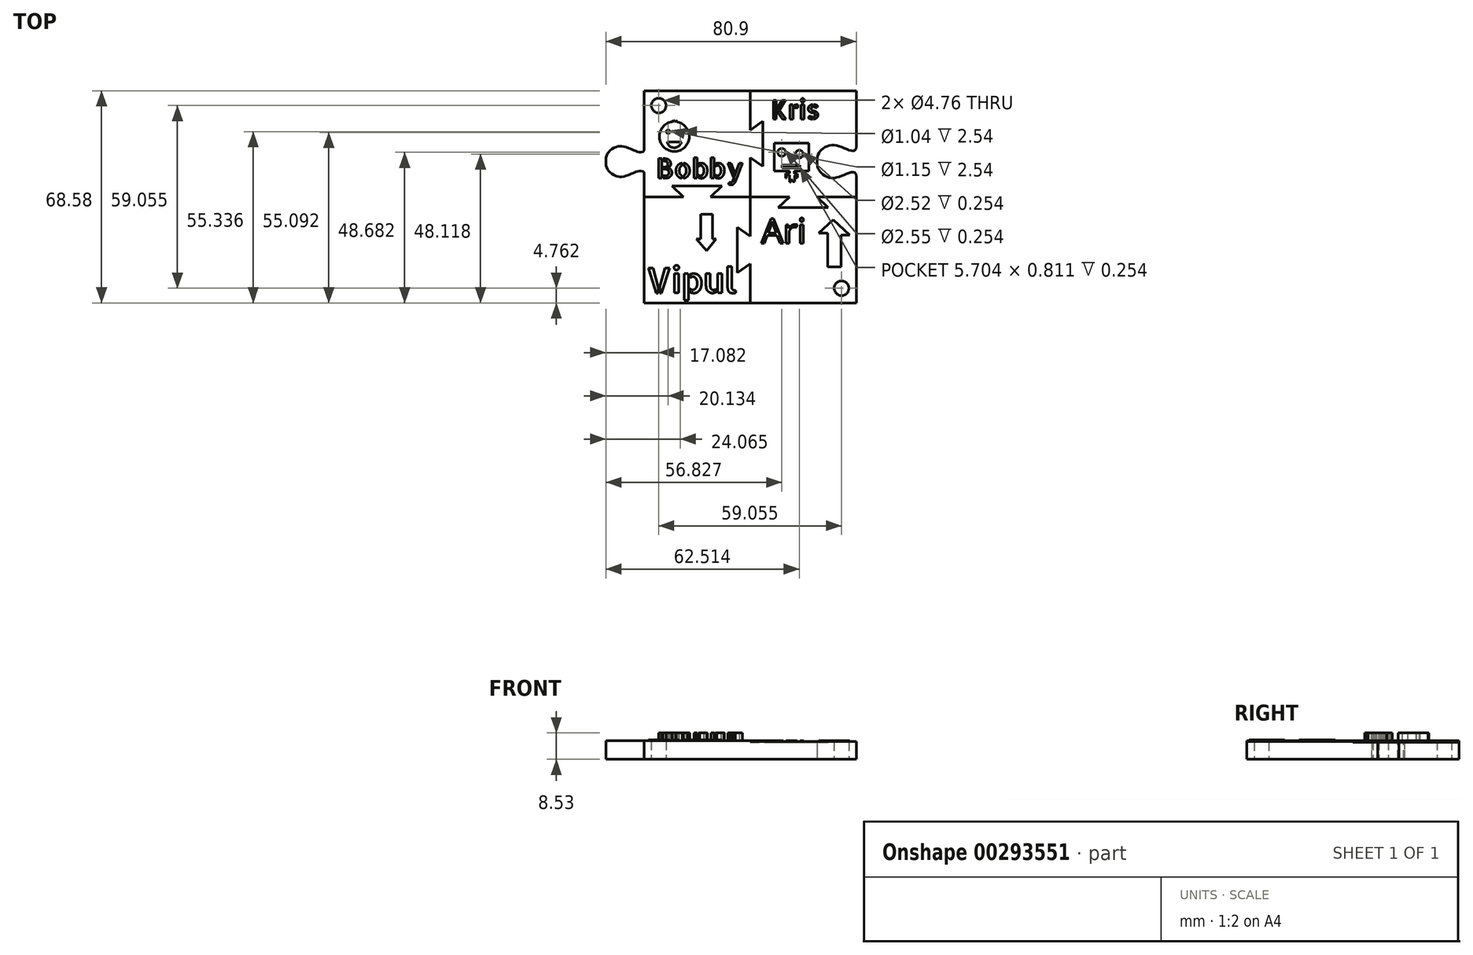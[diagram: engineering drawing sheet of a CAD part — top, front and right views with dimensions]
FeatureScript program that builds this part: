
annotation { "Feature Type Name" : "Feature", "Feature Type Description" : "" }
export const myFeature = defineFeature(function(context is Context, id is Id, definition is map)
    precondition{}
    {
        {
            var Q0;
            Q0=qCreatedBy(makeId("Top.planeOp"),FACE);
            var sketch = newSketch(context, id + "F0", { "sketchPlane" : qUnion([Q0])});
            skLineSegment(sketch, "E0.bottom", {"start": v(34.3, 34.3) * mm, "end": v(-34.3, 34.3) * mm});
            skLineSegment(sketch, "E0.top", {"start": v(34.3, -34.3) * mm, "end": v(-34.3, -34.3) * mm});
            skLineSegment(sketch, "E0.left", {"start": v(34.3, 34.3) * mm, "end": v(34.3, -34.3) * mm});
            skLineSegment(sketch, "E0.right", {"start": v(-34.3, 34.3) * mm, "end": v(-34.3, -34.3) * mm});
            skPoint(sketch, "E0.middle", {"position": v(0, 0) * mm});
            skCircle(sketch, "E1", {"center": v(-29.53, 29.53) * mm, "radius": 2.38 * mm});
            skCircle(sketch, "E2.MirrorC", {"center": v(29.53, -29.53) * mm, "radius": 2.38 * mm});
            skSolve(sketch);
        }
        {
            var Q0;
            Q0=qSketchRegion(id+"F0",true);
            extrude(context, id + "F1", {"entities" : qUnion([Q0]), "depth" : 3.17 * mm});
        }
        {
            var Q0;
            Q0=qCreatedBy(makeId("Top.planeOp"),FACE);
            var sketch = newSketch(context, id + "F2", { "sketchPlane" : qUnion([Q0])});
            skPoint(sketch, "E3", {"position": v(-34.3, 16.33) * mm});
            skPoint(sketch, "E4", {"position": v(-36.2, 14.99) * mm});
            skPoint(sketch, "E5", {"position": v(-41.66, 16.76) * mm});
            skPoint(sketch, "E6", {"position": v(-45.72, 14.99) * mm});
            skPoint(sketch, "E7", {"position": v(-47, 11.43) * mm});
            skFitSpline(sketch, "E8", {"points": [v(-34.3, 16.33) * mm, v(-36.2, 14.99) * mm, v(-41.66, 16.76) * mm, v(-45.72, 14.99) * mm, v(-47, 11.43) * mm], "startDerivative": vector(0, -24.54) * mm, "endDerivative": vector(0, -20.15) * mm});
            skLineSegment(sketch, "E9", {"start": v(-47, 11.43) * mm, "end": v(-29.95, 11.43) * mm, "construction": true});
            skFitSpline(sketch, "E10.MirrorCS", {"points": [v(-34.3, 6.53) * mm, v(-36.2, 7.87) * mm, v(-41.66, 6.1) * mm, v(-45.72, 7.87) * mm, v(-47, 11.43) * mm], "startDerivative": vector(0, 24.54) * mm, "endDerivative": vector(0, 20.15) * mm});
            skLineSegment(sketch, "E11", {"start": v(-34.3, 16.33) * mm, "end": v(-34.3, 6.53) * mm, "construction": true});
            skFitSpline(sketch, "E12.MirrorCS", {"points": [v(-34.3, 16.33) * mm, v(-32.39, 14.99) * mm, v(-26.92, 16.76) * mm, v(-22.86, 14.99) * mm, v(-21.59, 11.43) * mm], "startDerivative": vector(0, -24.54) * mm, "endDerivative": vector(0, -20.15) * mm});
            skFitSpline(sketch, "E13.MirrorCS", {"points": [v(-34.3, 6.53) * mm, v(-32.39, 7.87) * mm, v(-26.92, 6.1) * mm, v(-22.86, 7.87) * mm, v(-21.59, 11.43) * mm], "startDerivative": vector(0, 24.54) * mm, "endDerivative": vector(0, 20.15) * mm});
            skFitSpline(sketch, "E14.0", {"points": [v(-33.9, 6.53) * mm, v(-33.9, 6.8) * mm, v(-33.96, 7.3) * mm, v(-34.16, 7.77) * mm, v(-34.42, 8.07) * mm, v(-34.73, 8.28) * mm, v(-35.16, 8.4) * mm, v(-35.7, 8.38) * mm, v(-36.22, 8.27) * mm, v(-36.76, 8.1) * mm, v(-37.5, 7.83) * mm, v(-38.44, 7.42) * mm, v(-39.6, 6.94) * mm, v(-40.54, 6.64) * mm, v(-41.28, 6.5) * mm, v(-41.8, 6.46) * mm, v(-42.32, 6.5) * mm, v(-43, 6.62) * mm, v(-43.8, 6.91) * mm, v(-44.68, 7.44) * mm, v(-45.29, 7.96) * mm, v(-45.69, 8.4) * mm, v(-46.02, 8.85) * mm, v(-46.33, 9.45) * mm, v(-46.56, 10.3) * mm, v(-46.6, 11.03) * mm, v(-46.6, 11.43) * mm]});
            skFitSpline(sketch, "E14.1", {"points": [v(-33.9, 16.33) * mm, v(-33.9, 16.05) * mm, v(-33.96, 15.56) * mm, v(-34.16, 15.09) * mm, v(-34.42, 14.8) * mm, v(-34.73, 14.58) * mm, v(-35.16, 14.46) * mm, v(-35.7, 14.48) * mm, v(-36.22, 14.6) * mm, v(-36.76, 14.76) * mm, v(-37.5, 15.03) * mm, v(-38.44, 15.44) * mm, v(-39.6, 15.92) * mm, v(-40.54, 16.22) * mm, v(-41.28, 16.36) * mm, v(-41.8, 16.4) * mm, v(-42.32, 16.37) * mm, v(-43, 16.24) * mm, v(-43.8, 15.95) * mm, v(-44.68, 15.42) * mm, v(-45.29, 14.9) * mm, v(-45.69, 14.46) * mm, v(-46.02, 14.01) * mm, v(-46.33, 13.41) * mm, v(-46.56, 12.55) * mm, v(-46.6, 11.83) * mm, v(-46.6, 11.43) * mm]});
            skLineSegment(sketch, "E15", {"start": v(-34.3, 16.33) * mm, "end": v(-34.3, 6.53) * mm});
            skLineSegment(sketch, "E16", {"start": v(-34.3, 7.92) * mm, "end": v(-34.3, 14.94) * mm});
            skFitSpline(sketch, "E17.MirrorCS", {"points": [v(34.3, 16.33) * mm, v(32.39, 14.99) * mm, v(26.92, 16.76) * mm, v(22.86, 14.99) * mm, v(21.59, 11.43) * mm], "startDerivative": vector(0, -24.54) * mm, "endDerivative": vector(0, -20.15) * mm});
            skFitSpline(sketch, "E18.MirrorCS", {"points": [v(34.3, 6.53) * mm, v(32.39, 7.87) * mm, v(26.92, 6.1) * mm, v(22.86, 7.87) * mm, v(21.59, 11.43) * mm], "startDerivative": vector(0, 24.54) * mm, "endDerivative": vector(0, 20.15) * mm});
            skLineSegment(sketch, "E19", {"start": v(34.3, 16.33) * mm, "end": v(39.12, 16.33) * mm});
            skLineSegment(sketch, "E20", {"start": v(39.12, 16.33) * mm, "end": v(39.12, 6.53) * mm});
            skLineSegment(sketch, "E21", {"start": v(39.12, 6.53) * mm, "end": v(34.3, 6.53) * mm});
            skSolve(sketch);
        }
        {
            var Q0;
            Q0=makeQuery(id+"F2.imprint","IMPRINT",FACE,{"disambiguationData":[TD([[makeQuery(id+"F2.imprint","IMPRINT",EDGE,{"derivedFrom":sQuery(id+"F2.wireOp",EDGE,"E14.0")}),-1.0]])]});
            var Q1;
            Q1=makeQuery(id+"F1.opExtrude","CAP_FACE",FACE,{"disambiguationData":[OSD([sQuery(id+"F0.wireOp",EDGE,"E0.bottom"),sQuery(id+"F0.wireOp",EDGE,"E0.top"),sQuery(id+"F0.wireOp",EDGE,"E0.left"),sQuery(id+"F0.wireOp",EDGE,"E0.right"),sQuery(id+"F0.wireOp",EDGE,"E1"),sQuery(id+"F0.wireOp",EDGE,"e1648c08-8adf-473f-9b64-c467cf328ef90.MirrorC"),sQuery(id+"F0.wireOp",EDGE,"1cdcda55-2210-49d8-b5f0-9198a802923b0.MirrorC"),sQuery(id+"F0.wireOp",EDGE,"E2.MirrorC")])],"isStart":false});
            extrude(context, id + "F3", {"entities" : qUnion([Q0]), "operationType" : NewBodyOperationType.ADD, "endBound" : BoundingType.UP_TO_SURFACE, "endBoundEntityFace" : qUnion([Q1]), "depth" : 25.4 * mm});
        }
        {
            var Q0;
            Q0=qCreatedBy(makeId("Right.planeOp"),FACE);
            var sketch = newSketch(context, id + "F4", { "sketchPlane" : qUnion([Q0])});
            skLineSegment(sketch, "E22", {"start": v(0, -65.87) * mm, "end": v(0, 47.63) * mm});
            skSolve(sketch);
        }
        {
            var Q0;
            Q0=makeQuery(id+"F2.imprint","IMPRINT",FACE,{"disambiguationData":[TD([[makeQuery(id+"F2.imprint","IMPRINT",EDGE,{"derivedFrom":sQuery(id+"F2.wireOp",EDGE,"E17.MirrorCS")}),1.0]])]});
            extrude(context, id + "F5", {"entities" : qUnion([Q0]), "operationType" : NewBodyOperationType.REMOVE, "endBound" : BoundingType.THROUGH_ALL, "depth" : 25.4 * mm});
        }
        {
            var Q0;
            {var subQ0=sQuery(id+"F0.wireOp",EDGE,"E2.MirrorC");var subQ1=sQuery(id+"F0.wireOp",EDGE,"E1");var subQ2=sQuery(id+"F0.wireOp",EDGE,"E0.right");var subQ3=sQuery(id+"F0.wireOp",EDGE,"E0.left");var subQ4=sQuery(id+"F0.wireOp",EDGE,"E0.top");var subQ5=sQuery(id+"F0.wireOp",EDGE,"E0.bottom");Q0=makeQuery(id+"FDfX84p6046V9zH_1.3.F3.boolean.opBoolean","MERGE",FACE,{"derivedFrom":[makeQuery(id+"FDfX84p6046V9zH_1.2.F3.boolean.opBoolean","MERGE",FACE,{"derivedFrom":[makeQuery(id+"FDfX84p6046V9zH_1.1.F3.boolean.opBoolean","MERGE",FACE,{"derivedFrom":[makeQuery(id+"F3.boolean.opBoolean","MERGE",FACE,{"derivedFrom":[makeQuery(id+"F1.opExtrude","CAP_FACE",FACE,{"disambiguationData":[OSD([subQ5,subQ4,subQ3,subQ2,subQ1,subQ0])],"isStart":false}),makeQuery(id+"F3.opExtrude","CAP_FACE",FACE,{"disambiguationData":[OSD([subQ5,subQ4,subQ3,subQ2,subQ1,subQ0])],"isStart":false})]}),makeQuery(id+"FDfX84p6046V9zH_1.1.F3.opExtrude","CAP_FACE",FACE,{"disambiguationData":[OSD([subQ5,subQ4,subQ3,subQ2,subQ1,subQ0])],"isStart":false})]}),makeQuery(id+"FDfX84p6046V9zH_1.2.F3.opExtrude","CAP_FACE",FACE,{"disambiguationData":[OSD([subQ5,subQ4,subQ3,subQ2,subQ1,subQ0])],"isStart":false})]}),makeQuery(id+"FDfX84p6046V9zH_1.3.F3.opExtrude","CAP_FACE",FACE,{"disambiguationData":[OSD([subQ5,subQ4,subQ3,subQ2,subQ1,subQ0])],"isStart":false})]});}
            var sketch = newSketch(context, id + "F6", { "sketchPlane" : qUnion([Q0])});
            skLineSegment(sketch, "E23", {"start": v(-34.3, 0) * mm, "end": v(-21.58, 0) * mm});
            skLineSegment(sketch, "E24", {"start": v(-21.58, 0) * mm, "end": v(-25.25, 3.52) * mm});
            skLineSegment(sketch, "E25", {"start": v(0, 0) * mm, "end": v(-12.73, 0) * mm});
            skLineSegment(sketch, "E26", {"start": v(-12.73, 0) * mm, "end": v(-9.11, 3.52) * mm});
            skLineSegment(sketch, "E27", {"start": v(-9.11, 3.52) * mm, "end": v(-25.25, 3.52) * mm});
            skLineSegment(sketch, "E28.MirrorCS", {"start": v(34.3, 0) * mm, "end": v(21.58, 0) * mm});
            skLineSegment(sketch, "E29.MirrorCS", {"start": v(0, 0) * mm, "end": v(12.73, 0) * mm});
            skLineSegment(sketch, "E30.MirrorCS", {"start": v(9.11, -3.52) * mm, "end": v(25.25, -3.52) * mm});
            skLineSegment(sketch, "E31.MirrorCS", {"start": v(12.73, 0) * mm, "end": v(9.11, -3.52) * mm});
            skLineSegment(sketch, "E32.MirrorCS", {"start": v(21.58, 0) * mm, "end": v(25.25, -3.52) * mm});
            skPoint(sketch, "E33.MirrorCS.start.orphan", {"position": v(-12.73, 0) * mm});
            skPoint(sketch, "E34.MirrorCS.start.orphan", {"position": v(-21.58, 0) * mm});
            skLineSegment(sketch, "E35", {"start": v(0, 34.3) * mm, "end": v(0, 21.6) * mm});
            skLineSegment(sketch, "E36", {"start": v(0, 21.6) * mm, "end": v(4.16, 24.51) * mm});
            skLineSegment(sketch, "E37", {"start": v(0, 0) * mm, "end": v(0, 12.7) * mm});
            skLineSegment(sketch, "E38", {"start": v(0, 12.7) * mm, "end": v(4.16, 9.86) * mm});
            skLineSegment(sketch, "E39", {"start": v(4.16, 9.86) * mm, "end": v(4.16, 24.51) * mm});
            skLineSegment(sketch, "E40.MirrorCS", {"start": v(0, 0) * mm, "end": v(0, -12.7) * mm});
            skLineSegment(sketch, "E41.MirrorCS", {"start": v(0, -34.3) * mm, "end": v(0, -21.6) * mm});
            skLineSegment(sketch, "E42.MirrorCS", {"start": v(0, -12.7) * mm, "end": v(-4.16, -9.86) * mm});
            skLineSegment(sketch, "E43.MirrorCS", {"start": v(-4.16, -9.86) * mm, "end": v(-4.16, -24.51) * mm});
            skLineSegment(sketch, "E44.MirrorCS", {"start": v(0, -21.6) * mm, "end": v(-4.16, -24.51) * mm});
            skPoint(sketch, "E45.MirrorCS.start.orphan", {"position": v(0, -12.7) * mm});
            skPoint(sketch, "E46.MirrorCS.start.orphan", {"position": v(0, -21.6) * mm});
            skSolve(sketch);
        }
        {
            var Q0;
            {var subQ1=sQuery(id+"F6.wireOp",EDGE,"E28.MirrorCS");Q0=makeQuery(id+"F6.imprint","IMPRINT",FACE,{"disambiguationData":[TD([[makeQuery(id+"F6.imprint","IMPRINT",EDGE,{"derivedFrom":subQ1}),1.0]])]});}
            extrude(context, id + "F7", {"entities" : qUnion([Q0]), "operationType" : NewBodyOperationType.ADD, "depth" : 2.54 * mm});
        }
        {
            var Q0;
            {var subQ22=sQuery(id+"F6.wireOp",EDGE,"E23");Q0=makeQuery(id+"F6.imprint","IMPRINT",FACE,{"disambiguationData":[TD([[makeQuery(id+"F6.imprint","IMPRINT",EDGE,{"derivedFrom":subQ22}),-1.0]])]});}
            extrude(context, id + "F8", {"entities" : qUnion([Q0]), "operationType" : NewBodyOperationType.ADD, "depth" : 2.8 * mm});
        }
        {
            var Q0;
            {var subQ21=sQuery(id+"F6.wireOp",EDGE,"E23");Q0=makeQuery(id+"F6.imprint","IMPRINT",FACE,{"disambiguationData":[TD([[makeQuery(id+"F6.imprint","IMPRINT",EDGE,{"derivedFrom":subQ21}),1.0]])]});}
            extrude(context, id + "F9", {"entities" : qUnion([Q0]), "operationType" : NewBodyOperationType.ADD, "depth" : 2.82 * mm});
        }
        {
            var Q0;
            {var subQ0=sQuery(id+"F0.wireOp",EDGE,"E2.MirrorC");var subQ1=sQuery(id+"F0.wireOp",EDGE,"E1");var subQ2=sQuery(id+"F0.wireOp",EDGE,"E0.right");var subQ3=sQuery(id+"F0.wireOp",EDGE,"E0.left");var subQ4=sQuery(id+"F0.wireOp",EDGE,"E0.top");var subQ5=sQuery(id+"F0.wireOp",EDGE,"E0.bottom");Q0=makeQuery(id+"FDfX84p6046V9zH_1.3.F3.boolean.opBoolean","MERGE",FACE,{"derivedFrom":[makeQuery(id+"FDfX84p6046V9zH_1.2.F3.boolean.opBoolean","MERGE",FACE,{"derivedFrom":[makeQuery(id+"FDfX84p6046V9zH_1.1.F3.boolean.opBoolean","MERGE",FACE,{"derivedFrom":[makeQuery(id+"F3.boolean.opBoolean","MERGE",FACE,{"derivedFrom":[makeQuery(id+"F1.opExtrude","CAP_FACE",FACE,{"disambiguationData":[OSD([subQ5,subQ4,subQ3,subQ2,subQ1,subQ0])],"isStart":false}),makeQuery(id+"F3.opExtrude","CAP_FACE",FACE,{"disambiguationData":[OSD([subQ5,subQ4,subQ3,subQ2,subQ1,subQ0])],"isStart":false})]}),makeQuery(id+"FDfX84p6046V9zH_1.1.F3.opExtrude","CAP_FACE",FACE,{"disambiguationData":[OSD([subQ5,subQ4,subQ3,subQ2,subQ1,subQ0])],"isStart":false})]}),makeQuery(id+"FDfX84p6046V9zH_1.2.F3.opExtrude","CAP_FACE",FACE,{"disambiguationData":[OSD([subQ5,subQ4,subQ3,subQ2,subQ1,subQ0])],"isStart":false})]}),makeQuery(id+"FDfX84p6046V9zH_1.3.F3.opExtrude","CAP_FACE",FACE,{"disambiguationData":[OSD([subQ5,subQ4,subQ3,subQ2,subQ1,subQ0])],"isStart":false})]});}
            extrude(context, id + "F10", {"entities" : qUnion([Q0]), "operationType" : NewBodyOperationType.ADD, "depth" : 2.3 * mm});
        }
        {
            var Q0;
            Q0=makeQuery(id+"F8.opExtrude","CAP_FACE",FACE,{"disambiguationData":[OSD([sQuery(id+"F0.wireOp",EDGE,"E0.bottom"),sQuery(id+"F0.wireOp",EDGE,"E0.top"),sQuery(id+"F0.wireOp",EDGE,"E0.left"),sQuery(id+"F0.wireOp",EDGE,"E0.right"),sQuery(id+"F0.wireOp",EDGE,"E1"),sQuery(id+"F0.wireOp",EDGE,"E2.MirrorC"),sQuery(id+"F2.wireOp",EDGE,"E14.0"),sQuery(id+"F2.wireOp",EDGE,"E14.1"),sQuery(id+"F2.wireOp",EDGE,"E17.MirrorCS"),sQuery(id+"F2.wireOp",EDGE,"E18.MirrorCS"),sQuery(id+"F6.wireOp",EDGE,"E23"),sQuery(id+"F6.wireOp",EDGE,"E24"),sQuery(id+"F6.wireOp",EDGE,"E25"),sQuery(id+"F6.wireOp",EDGE,"E26"),sQuery(id+"F6.wireOp",EDGE,"E27"),sQuery(id+"F6.wireOp",EDGE,"E40.MirrorCS"),sQuery(id+"F6.wireOp",EDGE,"E41.MirrorCS"),sQuery(id+"F6.wireOp",EDGE,"E42.MirrorCS"),sQuery(id+"F6.wireOp",EDGE,"E43.MirrorCS"),sQuery(id+"F6.wireOp",EDGE,"E44.MirrorCS")])],"isStart":false});
            var sketch = newSketch(context, id + "F11", { "sketchPlane" : qUnion([Q0])});
            skText(sketch, "E47", { "text": "Vipul", "fontName": "AllertaStencil-Regular.ttf"});
            skLineSegment(sketch, "E48", {"start": v(-15.92, -5.68) * mm, "end": v(-12.2, -5.68) * mm});
            skLineSegment(sketch, "E49", {"start": v(-12.2, -5.68) * mm, "end": v(-12.2, -13.66) * mm});
            skLineSegment(sketch, "E50", {"start": v(-15.92, -5.68) * mm, "end": v(-15.92, -13.66) * mm});
            skLineSegment(sketch, "E51", {"start": v(-15.92, -13.66) * mm, "end": v(-17.34, -13.66) * mm});
            skLineSegment(sketch, "E52", {"start": v(-17.34, -13.66) * mm, "end": v(-14.06, -17.38) * mm});
            skPoint(sketch, "E52.endSnap0", {"position": v(-14.06, -5.68) * mm});
            skLineSegment(sketch, "E53", {"start": v(-14.06, -17.38) * mm, "end": v(-11, -13.66) * mm});
            skLineSegment(sketch, "E54", {"start": v(-11, -13.66) * mm, "end": v(-12.2, -13.66) * mm});
            const initialGuessF11  = {"E47": [-0.03353, -0.03106, 1, 0, 0.0081]};
            skSetInitialGuess(sketch, initialGuessF11);
            skSolve(sketch);
        }
        {
            var Q0;
            Q0 = qSketchRegion(id + "F11", true);
            extrude(context, id + "F12", {"entities" : qUnion([Q0]), "operationType" : NewBodyOperationType.ADD, "depth" : 0.25 * mm});
        }
        {
            var Q0;
            Q0=makeQuery(id+"F9.opExtrude","CAP_FACE",FACE,{"disambiguationData":[OSD([sQuery(id+"F0.wireOp",EDGE,"E0.bottom"),sQuery(id+"F0.wireOp",EDGE,"E0.top"),sQuery(id+"F0.wireOp",EDGE,"E0.left"),sQuery(id+"F0.wireOp",EDGE,"E0.right"),sQuery(id+"F0.wireOp",EDGE,"E1"),sQuery(id+"F0.wireOp",EDGE,"E2.MirrorC"),sQuery(id+"F2.wireOp",EDGE,"E14.0"),sQuery(id+"F2.wireOp",EDGE,"E14.1"),sQuery(id+"F2.wireOp",EDGE,"E17.MirrorCS"),sQuery(id+"F2.wireOp",EDGE,"E18.MirrorCS"),sQuery(id+"F6.wireOp",EDGE,"E23"),sQuery(id+"F6.wireOp",EDGE,"E24"),sQuery(id+"F6.wireOp",EDGE,"E25"),sQuery(id+"F6.wireOp",EDGE,"E26"),sQuery(id+"F6.wireOp",EDGE,"E27"),sQuery(id+"F6.wireOp",EDGE,"E35"),sQuery(id+"F6.wireOp",EDGE,"E36"),sQuery(id+"F6.wireOp",EDGE,"E37"),sQuery(id+"F6.wireOp",EDGE,"E38"),sQuery(id+"F6.wireOp",EDGE,"E39")])],"isStart":false});
            var sketch = newSketch(context, id + "F13", { "sketchPlane" : qUnion([Q0])});
            skText(sketch, "E55", { "text": "Bobby", "fontName": "AllertaStencil-Regular.ttf"});
            skCircle(sketch, "E56", {"center": v(-24.48, 19.5) * mm, "radius": 4.83 * mm});
            skCircle(sketch, "E57", {"center": v(-26.48, 21.05) * mm, "radius": 0.58 * mm});
            skCircle(sketch, "E58", {"center": v(-22.54, 20.8) * mm, "radius": 0.52 * mm});
            skLineSegment(sketch, "E59", {"start": v(-25.13, 24.28) * mm, "end": v(-25.15, 24.53) * mm});
            skLineSegment(sketch, "E60", {"start": v(-25.15, 24.53) * mm, "end": v(-24.88, 24.55) * mm});
            skLineSegment(sketch, "E61", {"start": v(-24.88, 24.55) * mm, "end": v(-24.88, 24.3) * mm});
            skLineSegment(sketch, "E62", {"start": v(-24.88, 24.3) * mm, "end": v(-24.7, 24.32) * mm});
            skLineSegment(sketch, "E63", {"start": v(-24.7, 24.32) * mm, "end": v(-24.7, 24.56) * mm});
            skLineSegment(sketch, "E64", {"start": v(-24.7, 24.56) * mm, "end": v(-24.31, 24.56) * mm});
            skLineSegment(sketch, "E65", {"start": v(-24.31, 24.56) * mm, "end": v(-24.36, 24.32) * mm});
            skLineSegment(sketch, "E66", {"start": v(-24.36, 24.32) * mm, "end": v(-24.05, 24.3) * mm});
            skLineSegment(sketch, "E67", {"start": v(-24.05, 24.3) * mm, "end": v(-24.05, 24.53) * mm});
            skLineSegment(sketch, "E68", {"start": v(-24.05, 24.53) * mm, "end": v(-23.41, 24.49) * mm});
            skLineSegment(sketch, "E69", {"start": v(-23.41, 24.49) * mm, "end": v(-23.53, 24.23) * mm});
            skLineSegment(sketch, "E70", {"start": v(-24.48, 17.68) * mm, "end": v(-26.76, 17.68) * mm});
            skLineSegment(sketch, "E71", {"start": v(-24.48, 17.68) * mm, "end": v(-22.2, 17.68) * mm});
            skArc(sketch, "E72", {"start": v(-26.76, 17.68) * mm, "mid": v(-24.49, 15.89) * mm, "end": v(-22.2, 17.68) * mm});
            const initialGuessF13  = {"E55": [-0.03036, 0.00603, 1, 0, 0.00634]};
            skSetInitialGuess(sketch, initialGuessF13);
            skSolve(sketch);
        }
        {
            var Q0;
            Q0 = qSketchRegion(id + "F13", true);
            extrude(context, id + "F14", {"entities" : qUnion([Q0]), "operationType" : NewBodyOperationType.ADD, "depth" : 2.54 * mm});
        }
        {
            var Q0;
            Q0=makeQuery(id+"F10.opExtrude","CAP_FACE",FACE,{"disambiguationData":[OSD([sQuery(id+"F0.wireOp",EDGE,"E0.bottom"),sQuery(id+"F0.wireOp",EDGE,"E0.top"),sQuery(id+"F0.wireOp",EDGE,"E0.left"),sQuery(id+"F0.wireOp",EDGE,"E0.right"),sQuery(id+"F0.wireOp",EDGE,"E1"),sQuery(id+"F0.wireOp",EDGE,"E2.MirrorC")])],"isStart":false});
            var sketch = newSketch(context, id + "F15", { "sketchPlane" : qUnion([Q0])});
            skText(sketch, "E73", { "text": "Kris", "fontName": "AllertaStencil-Regular.ttf"});
            skLineSegment(sketch, "E74.bottom", {"start": v(7.79, 17.39) * mm, "end": v(18.99, 17.39) * mm});
            skLineSegment(sketch, "E74.top", {"start": v(7.79, 8.36) * mm, "end": v(18.99, 8.36) * mm});
            skLineSegment(sketch, "E74.left", {"start": v(7.79, 17.39) * mm, "end": v(7.79, 8.36) * mm});
            skLineSegment(sketch, "E74.right", {"start": v(18.99, 17.39) * mm, "end": v(18.99, 8.36) * mm});
            skCircle(sketch, "E75", {"center": v(10.22, 14.4) * mm, "radius": 1.28 * mm});
            skCircle(sketch, "E76", {"center": v(15.9, 13.83) * mm, "radius": 1.26 * mm});
            skLineSegment(sketch, "E77", {"start": v(10.34, 10.4) * mm, "end": v(10.34, 9.38) * mm});
            skLineSegment(sketch, "E78", {"start": v(10.34, 9.38) * mm, "end": v(16.04, 9.38) * mm});
            skLineSegment(sketch, "E79", {"start": v(16.04, 9.38) * mm, "end": v(16.04, 10.2) * mm});
            skLineSegment(sketch, "E80", {"start": v(16.04, 10.2) * mm, "end": v(10.34, 10.2) * mm});
            skLineSegment(sketch, "E81", {"start": v(12.77, 8.36) * mm, "end": v(12.77, 7.52) * mm});
            skLineSegment(sketch, "E82", {"start": v(12.77, 7.52) * mm, "end": v(11.48, 7.52) * mm});
            skLineSegment(sketch, "E83", {"start": v(11.48, 7.52) * mm, "end": v(11.48, 6.05) * mm});
            skLineSegment(sketch, "E84", {"start": v(11.48, 6.05) * mm, "end": v(11.78, 6.05) * mm});
            skLineSegment(sketch, "E85", {"start": v(11.78, 6.05) * mm, "end": v(11.78, 7.02) * mm});
            skLineSegment(sketch, "E86", {"start": v(11.78, 7.02) * mm, "end": v(12.73, 7.02) * mm});
            skLineSegment(sketch, "E87", {"start": v(12.73, 7.02) * mm, "end": v(12.73, 6) * mm});
            skLineSegment(sketch, "E88", {"start": v(12.73, 6) * mm, "end": v(14.43, 6) * mm});
            skLineSegment(sketch, "E89", {"start": v(14.43, 6) * mm, "end": v(14.43, 6.9) * mm});
            skLineSegment(sketch, "E90", {"start": v(14.43, 6.9) * mm, "end": v(14.97, 6.9) * mm});
            skLineSegment(sketch, "E91", {"start": v(14.97, 6.9) * mm, "end": v(14.97, 6.2) * mm});
            skLineSegment(sketch, "E92", {"start": v(14.97, 6.2) * mm, "end": v(15.36, 6.2) * mm});
            skLineSegment(sketch, "E93", {"start": v(15.36, 6.2) * mm, "end": v(15.36, 7.48) * mm});
            skLineSegment(sketch, "E94", {"start": v(15.36, 7.48) * mm, "end": v(14.34, 7.48) * mm});
            skLineSegment(sketch, "E95", {"start": v(14.34, 7.48) * mm, "end": v(14.34, 8.36) * mm});
            skLineSegment(sketch, "E96", {"start": v(12.73, 6) * mm, "end": v(12.73, 4.84) * mm});
            skLineSegment(sketch, "E97", {"start": v(12.73, 4.84) * mm, "end": v(13.27, 4.84) * mm});
            skLineSegment(sketch, "E98", {"start": v(13.27, 4.84) * mm, "end": v(13.27, 5.44) * mm});
            skLineSegment(sketch, "E99", {"start": v(13.27, 5.44) * mm, "end": v(13.8, 5.44) * mm});
            skLineSegment(sketch, "E100", {"start": v(13.8, 5.44) * mm, "end": v(13.8, 4.86) * mm});
            skLineSegment(sketch, "E101", {"start": v(13.8, 4.86) * mm, "end": v(14.42, 4.86) * mm});
            skLineSegment(sketch, "E102", {"start": v(14.42, 4.86) * mm, "end": v(14.43, 6) * mm});
            const initialGuessF15  = {"E73": [0.00674, 0.02516, 1, 0, 0.006]};
            skSetInitialGuess(sketch, initialGuessF15);
            skSolve(sketch);
        }
        {
            var Q0;
            Q0 = qSketchRegion(id + "F15", true);
            extrude(context, id + "F16", {"entities" : qUnion([Q0]), "operationType" : NewBodyOperationType.ADD, "depth" : 0.25 * mm});
        }
        {
            var Q0;
            Q0=makeQuery(id+"F7.opExtrude","CAP_FACE",FACE,{"disambiguationData":[OSD([sQuery(id+"F0.wireOp",EDGE,"E0.bottom"),sQuery(id+"F0.wireOp",EDGE,"E0.top"),sQuery(id+"F0.wireOp",EDGE,"E0.left"),sQuery(id+"F0.wireOp",EDGE,"E0.right"),sQuery(id+"F0.wireOp",EDGE,"E1"),sQuery(id+"F0.wireOp",EDGE,"E2.MirrorC"),sQuery(id+"F2.wireOp",EDGE,"E14.0"),sQuery(id+"F2.wireOp",EDGE,"E14.1"),sQuery(id+"F2.wireOp",EDGE,"E17.MirrorCS"),sQuery(id+"F2.wireOp",EDGE,"E18.MirrorCS"),sQuery(id+"F6.wireOp",EDGE,"E28.MirrorCS"),sQuery(id+"F6.wireOp",EDGE,"E29.MirrorCS"),sQuery(id+"F6.wireOp",EDGE,"E30.MirrorCS"),sQuery(id+"F6.wireOp",EDGE,"E31.MirrorCS"),sQuery(id+"F6.wireOp",EDGE,"E32.MirrorCS"),sQuery(id+"F6.wireOp",EDGE,"E40.MirrorCS"),sQuery(id+"F6.wireOp",EDGE,"E41.MirrorCS"),sQuery(id+"F6.wireOp",EDGE,"E42.MirrorCS"),sQuery(id+"F6.wireOp",EDGE,"E43.MirrorCS"),sQuery(id+"F6.wireOp",EDGE,"E44.MirrorCS")])],"isStart":false});
            var sketch = newSketch(context, id + "F17", { "sketchPlane" : qUnion([Q0])});
            skText(sketch, "E103", { "text": "Ari", "fontName": "OpenSans-Regular.ttf"});
            skLineSegment(sketch, "E104", {"start": v(25.04, -22.6) * mm, "end": v(29.44, -22.6) * mm});
            skLineSegment(sketch, "E105", {"start": v(29.44, -22.6) * mm, "end": v(29.44, -12.4) * mm});
            skLineSegment(sketch, "E106", {"start": v(29.44, -12.4) * mm, "end": v(32.17, -12.4) * mm});
            skLineSegment(sketch, "E107", {"start": v(32.17, -12.4) * mm, "end": v(26.8, -7.46) * mm});
            skLineSegment(sketch, "E108", {"start": v(26.8, -7.46) * mm, "end": v(22.16, -11.78) * mm});
            skLineSegment(sketch, "E109", {"start": v(22.16, -11.78) * mm, "end": v(25.09, -11.78) * mm});
            skLineSegment(sketch, "E110", {"start": v(25.09, -11.78) * mm, "end": v(25.04, -22.6) * mm});
            const initialGuessF17  = {"E103": [0.00363, -0.01503, 1, 0, 0.00805]};
            skSetInitialGuess(sketch, initialGuessF17);
            skSolve(sketch);
        }
        {
            var Q0;
            Q0 = qSketchRegion(id + "F17", true);
            extrude(context, id + "F18", {"entities" : qUnion([Q0]), "operationType" : NewBodyOperationType.ADD, "depth" : 0.25 * mm});
        }
    });
